# Revit family: Shower-Bath_Shower-KOHLER-ALEO-K-72282T
name_source: partatom
category: Plumbing Fixtures
revit_build: Autodesk Revit 2017 (Build: 20160225_1515(x64)
units: mm (PartAtom-declared; Revit-internal decimal feet)

## family parameters
Cut with Voids When Loaded = No
Host = Face
OmniClass Number = 23.31.17.00
OmniClass Title = Showers
Part Type = Normal
Room Calculation Point = No
Round Connector Dimension = Use Diameter
Shared = No

## types (3) — shared parameters
ADA Compliant = No
Assembly Code = D2010700
CW Connection = Yes
Cold Water Inlet = Cold Water Inlet
Date Modified = 09/17/2020
Description = Wall-hung bathtub shower faucet
Drain Included = No
Flow Rate = 2 GPM
HW Connection = Yes
Handle Clearance = 3 5/8"
Height = 18 5/8"
Hot Water Inlet = Hot Water Inlet
Length = 9 13/16"
Manufacturer = KOHLER Co.
Master Format 2014 = 22 42 23
Master Format 2014 Name = Residential Showers
Material = Premium Metal Construction
Pressure = 80.00 psi
Product Name = Aleo
Spout Reach = 4 7/16"
URL = http://www.kohler.com.cn
Vent Connection = No
Waste Connection = No
Waste Water Outlet = Waste Water Outlet
WaterSense Certified = No
Width = 10 7/16"

## per-type parameters (varying)
| type | Default Elevation | Finish | Model | Product Documentation Link | Product Page URL | Type |
| CP- Polished Chrome | 36" | Kohler-Metal-CP-Polished_Chrome | K-72282T-4-CP | https://files.kohler.com.cn | https://www.kohler.com.cn | 1 |
| BL- Matte Black | 36" | Kohler-Metal-BL-Matte_Black | K-72282T-4-BL | https://files.kohler.com.cn | https://www.kohler.com.cn | 2 |
| 4E2, CP- Polished Chrome | 0" | Kohler-Metal-CP-Polished_Chrome | K-72282T-4E2-CP |  |  | 3 |

## geometry (parser evidence)
native form markers: Sweep x5
no freeform markers — native parametric forms only
